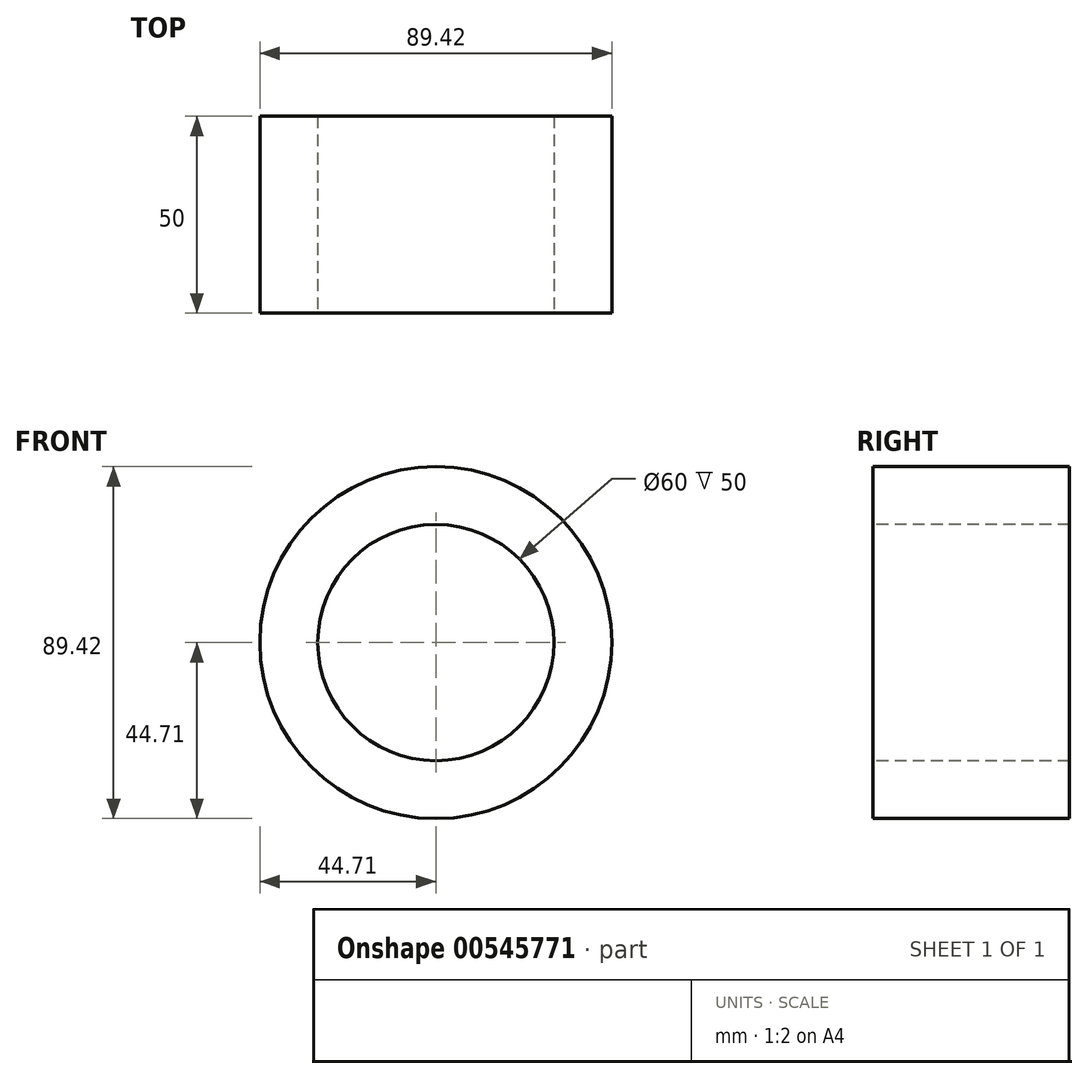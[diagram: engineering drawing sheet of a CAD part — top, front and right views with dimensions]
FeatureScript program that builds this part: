
annotation { "Feature Type Name" : "Feature", "Feature Type Description" : "" }
export const myFeature = defineFeature(function(context is Context, id is Id, definition is map)
    precondition{}
    {
        {
            var Q0;
            Q0=qCreatedBy(makeId("Front.planeOp"),FACE);
            var sketch = newSketch(context, id + "F0", { "sketchPlane" : qUnion([Q0])});
            skCircle(sketch, "E0", {"center": v(0, 0) * mm, "radius": 44.71 * mm});
            skSolve(sketch);
        }
        {
            var Q0;
            Q0=makeQuery(id+"F0.imprint","IMPRINT",FACE,{"disambiguationData":[TD([[makeQuery(id+"F0.imprint","IMPRINT",EDGE,{"derivedFrom":sQuery(id+"F0.wireOp",EDGE,"E0")}),1.0]])]});
            extrude(context, id + "F1", {"entities" : qUnion([Q0]), "depth" : 25 * mm, "offsetDistance" : 25 * mm});
        }
        {
            var Q0;
            Q0=makeQuery(id+"F1.opExtrude","SWEPT_BODY",BODY,{"disambiguationData":[OSD([sQuery(id+"F0.wireOp",EDGE,"E0")])]});
            var Q1;
            Q1=makeQuery(id+"F1.opExtrude","CAP_FACE",FACE,{"disambiguationData":[OSD([sQuery(id+"F0.wireOp",EDGE,"E0")])],"isStart":true});
            mirror(context, id + "F2", {"operationType" : NewBodyOperationType.ADD, "entities" : qUnion([Q0]), "mirrorPlane" : qUnion([Q1])});
        }
        {
            var Q0;
            Q0=makeQuery(id+"F1.opExtrude","CAP_FACE",FACE,{"disambiguationData":[OSD([sQuery(id+"F0.wireOp",EDGE,"E0")])],"isStart":false});
            var sketch = newSketch(context, id + "F3", { "sketchPlane" : qUnion([Q0])});
            skCircle(sketch, "E1", {"center": v(0, 0) * mm, "radius": 30 * mm});
            skSolve(sketch);
        }
        {
            var Q0;
            Q0=makeQuery(id+"F3.imprint","IMPRINT",FACE,{"disambiguationData":[TD([[makeQuery(id+"F3.imprint","IMPRINT",EDGE,{"derivedFrom":sQuery(id+"F3.wireOp",EDGE,"E1")}),1.0]])]});
            extrude(context, id + "F4", {"entities" : qUnion([Q0]), "operationType" : NewBodyOperationType.REMOVE, "oppositeDirection" : true, "depth" : 50 * mm, "offsetDistance" : 25 * mm});
        }
    });
